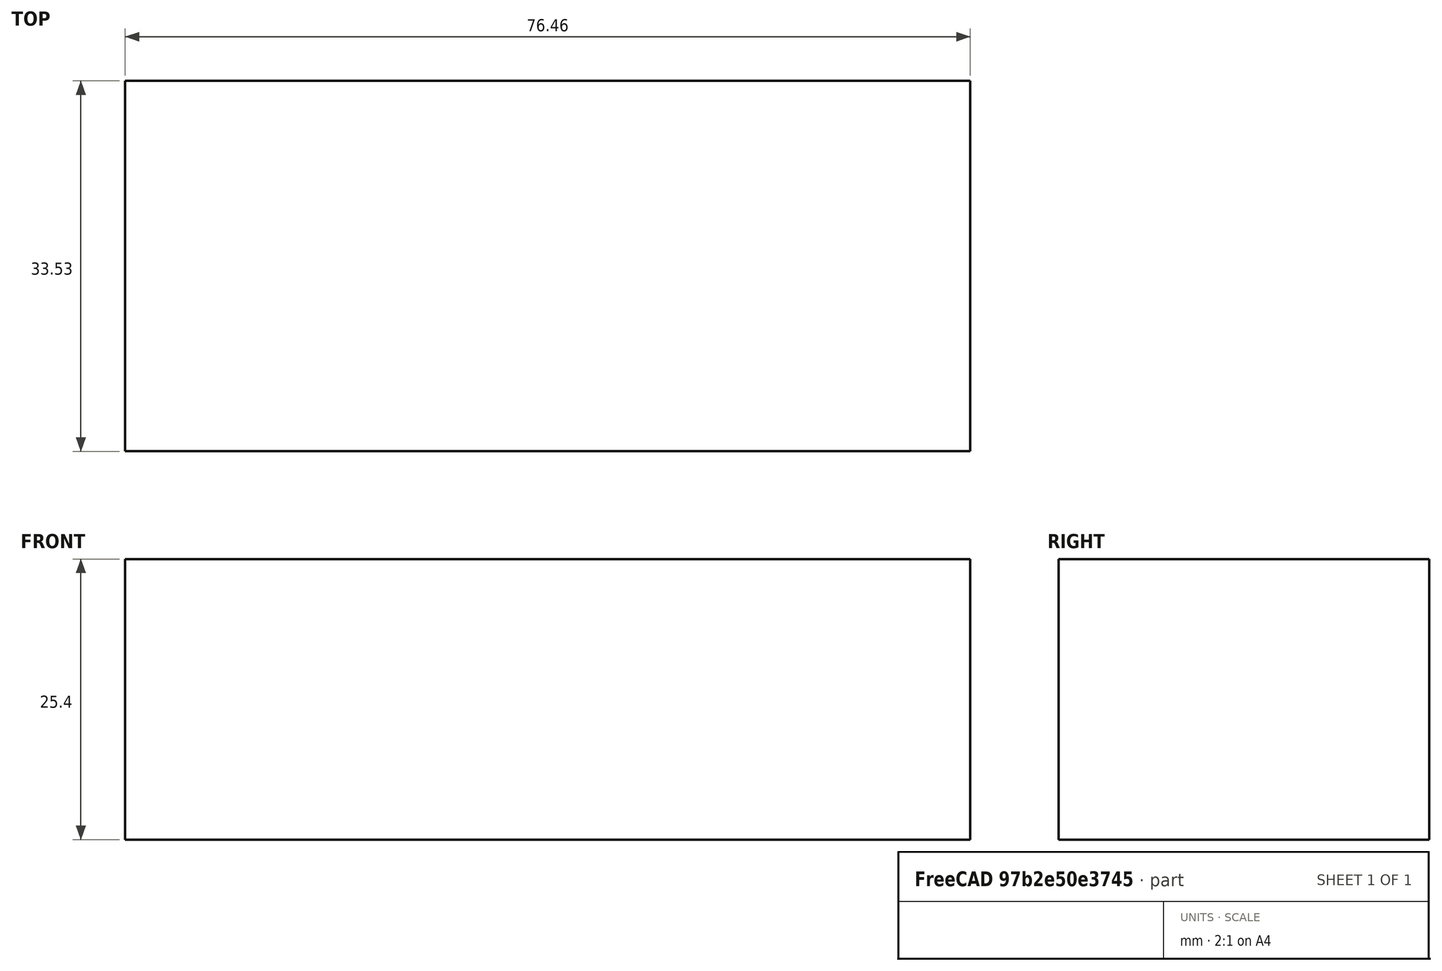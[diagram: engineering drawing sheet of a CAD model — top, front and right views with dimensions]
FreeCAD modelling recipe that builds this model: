
FCSTD DOCUMENT  (FreeCAD 1.0R38642 (Git))
Label: invalid_pads
License: All rights reserved
LicenseURL: http://en.wikipedia.org/wiki/All_rights_reserved
objects: Sketcher::SketchObject×1, PartDesign::Pad×1, PartDesign::Body×1
note: 6 computed .brp shape members not serialized (recipe doc carries the construction recipe); baked Part::Feature solids carry a one-line shape summary decoded from their .brp

FEATURE [Sketcher::SketchObject] Sketch  label="incomplete_rectangle"
  ArcFitTolerance = 1e-06
  AttachmentSupport = -> [XY_Plane]
  FullyConstrained = false
  MakeInternals = false
  MapMode = 5
  sketch-geometry (3):
    g0: LineSegment StartX=-45.8384 StartY=-16.5873 StartZ=0 EndX=30.6182 EndY=-16.5873 EndZ=0
    g1: LineSegment StartX=30.6182 StartY=-16.5873 StartZ=0 EndX=30.6182 EndY=16.9442 EndZ=0
    g2: LineSegment StartX=30.6182 StartY=16.9442 StartZ=0 EndX=-45.8384 EndY=16.9442 EndZ=0
  constraints (5):
    c: Coincident(g0,g1)
    c: Coincident(g1,g2)
    c: Vertical(g1)
    c: Horizontal(g0)
    c: Horizontal(g2)
FEATURE [PartDesign::Pad] Pad
  Direction = (0,0,1)
  Length = 25.4
  Length2 = 10
  Profile = -> Sketch
  ReferenceAxis = -> Sketch [N_Axis]
  Refine = true
  Suppressed = false
  Type = 0
FEATURE [PartDesign::Body] Body
  AllowCompound = false
  Group = -> [Sketch,Pad]
  Origin = -> Origin
  Tip = -> Pad
